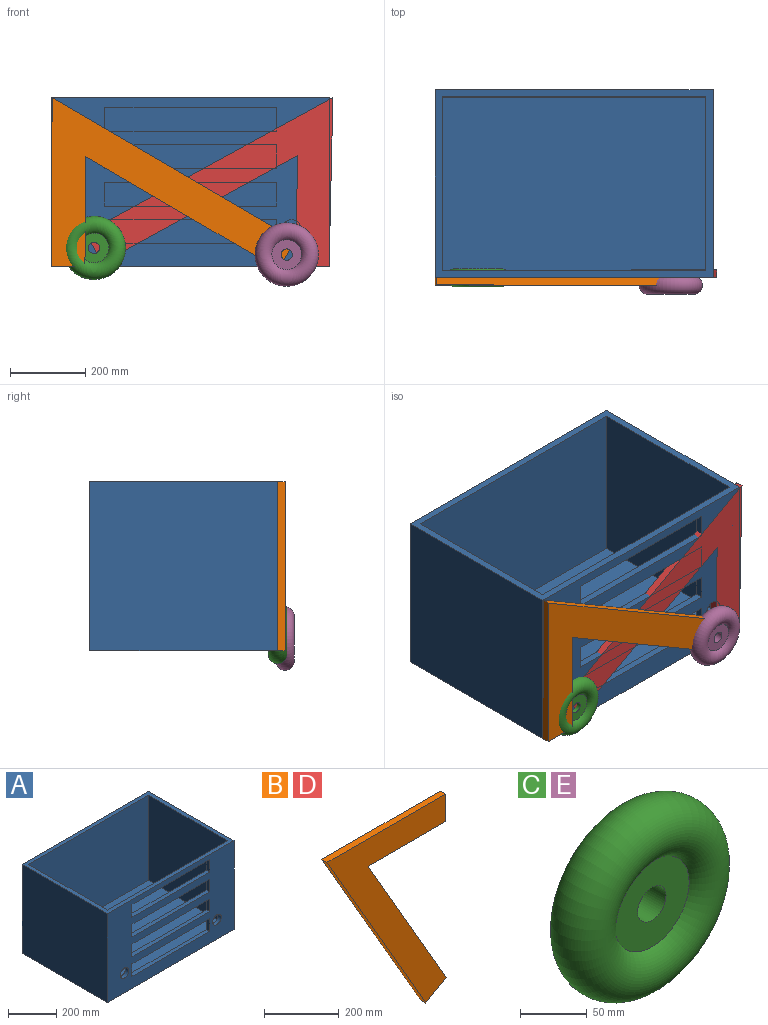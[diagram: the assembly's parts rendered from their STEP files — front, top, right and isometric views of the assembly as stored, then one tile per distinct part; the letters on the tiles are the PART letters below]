
ASSEMBLY  parts=5 mates=4
PART A: 29 faces, bbox 740x500x450 mm
  f0: plane 740x450mm, normal (0,-1,0), area 212822.6mm2, adj f2,f3,f4,f5,f11,f12,f13,f14
  f1: plane 702x431mm, normal (0,1,0), area 182384.6mm2, adj f2,f7,f8,f9,f11,f12,f13,f14
  f2: plane 740x500mm, normal (0,0,1), area 45676mm2, adj f0,f1,f3,f5,f6,f7,f9,f10
  f3: plane 500x450mm, normal (-1,0,0), area 225000mm2, adj f0,f2,f4,f6
  f4: plane 740x500mm, normal (0,0,-1), area 370000mm2, adj f0,f3,f5,f6
  f5: plane 500x450mm, normal (1,0,0), area 225000mm2, adj f0,f2,f4,f6
  f6: plane 740x450mm, normal (0,1,0), area 333000mm2, adj f2,f3,f4,f5
  f7: plane 462x431mm, normal (1,0,0), area 199122mm2, adj f1,f2,f8,f10
  f8: plane 702x462mm, normal (0,0,1), area 324324mm2, adj f1,f7,f9,f10
  f9: plane 462x431mm, normal (-1,0,0), area 199122mm2, adj f1,f2,f8,f10
  f10: plane 702x431mm, normal (0,-1,0), area 302562mm2, adj f2,f7,f8,f9
  f11: cylinder r=25mm len=50mm, axis (0,-1,0), area 2984.5mm2, adj f0,f1
  f12: cylinder r=25mm len=50mm, axis (0,-1,0), area 2984.5mm2, adj f0,f1
  f13: plane 63.71x19mm, normal (-1,0,0), area 1210.6mm2, adj f0,f1,f14,f16
  f14: plane 456.14x19mm, normal (0,0,-1), area 8666.7mm2, adj f0,f1,f13,f15
  f15: plane 63.71x19mm, normal (1,0,0), area 1210.6mm2, adj f0,f1,f14,f16
  f16: plane 456.14x19mm, normal (0,0,1), area 8666.7mm2, adj f0,f1,f13,f15
  f17: plane 63.71x19mm, normal (-1,0,0), area 1210.6mm2, adj f0,f1,f18,f20
  f18: plane 456.14x19mm, normal (0,0,-1), area 8666.7mm2, adj f0,f1,f17,f19
  f19: plane 63.71x19mm, normal (1,0,0), area 1210.6mm2, adj f0,f1,f18,f20
  f20: plane 456.14x19mm, normal (0,0,1), area 8666.7mm2, adj f0,f1,f17,f19
  f21: plane 63.71x19mm, normal (-1,0,0), area 1210.6mm2, adj f0,f1,f22,f24
  f22: plane 456.14x19mm, normal (0,0,-1), area 8666.7mm2, adj f0,f1,f21,f23
  f23: plane 63.71x19mm, normal (1,0,0), area 1210.6mm2, adj f0,f1,f22,f24
  f24: plane 456.14x19mm, normal (0,0,1), area 8666.7mm2, adj f0,f1,f21,f23
  f25: plane 456.14x19mm, normal (0,0,-1), area 8666.7mm2, adj f0,f1,f26,f28
  f26: plane 63.71x19mm, normal (1,0,0), area 1210.6mm2, adj f0,f1,f25,f27
  f27: plane 456.14x19mm, normal (0,0,1), area 8666.7mm2, adj f0,f1,f26,f28
  f28: plane 63.71x19mm, normal (-1,0,0), area 1210.6mm2, adj f0,f1,f25,f27
PART B: 8 faces, bbox 452.9x20x649.5 mm
  f0: plane 294.12x20mm, normal (0,0,-1), area 5882.3mm2, adj f1,f5,f6,f7
  f1: plane 90x20mm, normal (1,0,0), area 1800mm2, adj f0,f2,f6,f7
  f2: plane 450x20mm, normal (0,0,1), area 9000mm2, adj f1,f3,f6,f7
  f3: plane 649.52x375mm, normal (-0.87,0,-0.5), area 15000mm2, adj f2,f4,f6,f7
  f4: plane 77.94x45mm, normal (0.5,0,-0.87), area 1800mm2, adj f3,f5,f6,f7
  f5: plane 514.52x297.06mm, normal (0.87,0,0.5), area 11882.3mm2, adj f0,f4,f6,f7
  f6: plane 649.52x452.94mm, normal (0,-1,0), area 93970.4mm2, adj f0,f1,f2,f3,f4,f5
  f7: plane 649.52x452.94mm, normal (0,1,0), area 93970.4mm2, adj f0,f1,f2,f3,f4,f5
PART C: 4 faces, bbox 182.8x48.5x182.8 mm
  f0: torus R=60.18mm, axis (0,1,0), area 51524.3mm2, adj f1,f2
  f1: plane 78.78x78.78mm, normal (0,1,0), area 4167.6mm2, adj f0,f3
  f2: plane 78.78x78.78mm, normal (0,-1,0), area 4167.6mm2, adj f0,f3
  f3: cylinder r=15mm len=30mm, axis (0,-1,0), area 2356.2mm2, adj f1,f2
PART D: same geometry as B
PART E: same geometry as C
PLACE A t=(-370,250,0)mm
PLACE B rot(axis=(-0.7,0,0.71),180deg) t=(-693.66,-20,224.73)mm
PLACE C rot(axis=(0,-1,0),8.8deg) t=(-626.06,0,50.05)mm
PLACE D rot(axis=(0,1,0),91.3deg) t=(-39.95,20,225.95)mm
PLACE E rot(axis=(0,1,0),0.4deg) t=(-112.78,-20,32.29)mm
MATE revolute C.f3 <-> D.f6  axis (0,-1,0) through (-626.06,0,50.05)mm
MATE revolute E.f3 <-> B.f7  axis (0,-1,0) through (-112.78,-20,32.29)mm
MATE revolute D.f6 <-> A.f0  axis (0,-1,0) through (0,0,0)mm
MATE revolute B.f6 <-> A.f0  axis (0,1,0) through (-740,0,0)mm
